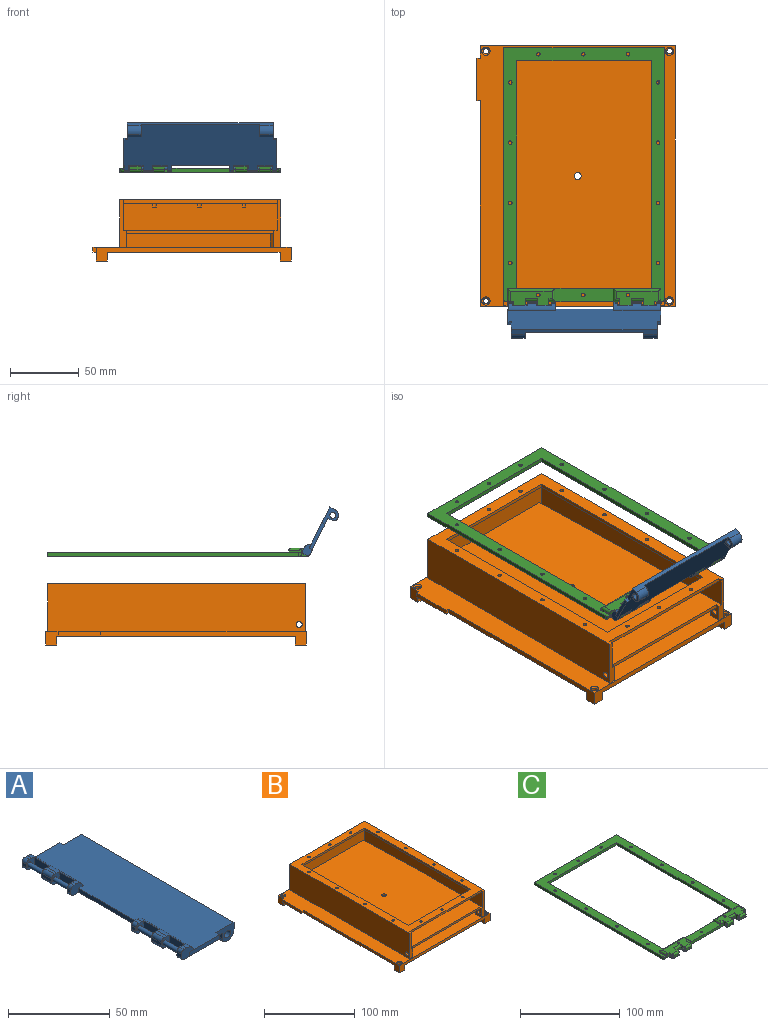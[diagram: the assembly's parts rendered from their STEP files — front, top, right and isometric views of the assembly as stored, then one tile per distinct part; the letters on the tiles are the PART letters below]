
ASSEMBLY  parts=3 mates=2
PART A: 74 faces, bbox 39.1x111x12.5 mm
  f0: plane 111x37.11mm, normal (0,0,-1), area 3582.4mm2, adj f13,f14,f15,f16,f17,f18,f19,f20
  f1: plane 3x1.73mm, normal (0,0,1), area 5.2mm2, adj f3,f17,f30,f59
  f2: plane 111x33.44mm, normal (0,0,1), area 3443.5mm2, adj f3,f13,f14,f15,f16,f32,f49,f57
  f3: cylinder r=5mm len=34mm, axis (0,1,0), area 175.9mm2, adj f1,f2,f9,f10,f13,f17,f18,f19
  f4: cylinder r=1.5mm len=3mm, axis (0,1,0), area 0.6mm2, adj f35,f56
  f5: cylinder r=1.25mm len=28.6mm, axis (0,-1,0), area 224.6mm2, adj f55,f56
  f6: cylinder r=1.5mm len=3mm, axis (0,1,0), area 0.4mm2, adj f38,f55
  f7: cylinder r=1.25mm len=28.5mm, axis (0,1,0), area 223.8mm2, adj f52,f53
  f8: cylinder r=1.5mm len=3mm, axis (0,1,0), area 4.7mm2, adj f17,f52
  f9: plane 2.5x1.73mm, normal (0,0,1), area 4.3mm2, adj f3,f13,f19,f29
  f10: plane 6.75x1.73mm, normal (0,0,1), area 11.7mm2, adj f3,f18,f21,f31
  f11: plane 3x1.9mm, normal (0,0,1), area 5.7mm2, adj f32,f35,f48,f49
  f12: plane 6.75x1.9mm, normal (0,0,1), area 12.8mm2, adj f40,f42,f46,f49
  f13: plane 8.5x6mm, normal (0,-1,0), area 37.3mm2, adj f0,f2,f3,f9,f16,f25,f26,f29
  f14: plane 8.67x6mm, normal (0,1,0), area 38.4mm2, adj f0,f2,f16,f33,f37,f44,f47,f49
  f15: plane 2.5x0.08mm, normal (-1,0,0), area 0.2mm2, adj f0,f2,f32,f62
  f16: plane 42.42x2.5mm, normal (-1,0,0), area 106mm2, adj f0,f2,f13,f14
  f17: plane 6x5.5mm, normal (0,-1,0), area 24mm2, adj f0,f1,f3,f8,f20,f24,f27,f30
  f18: plane 6x5.5mm, normal (0,1,0), area 24mm2, adj f0,f3,f10,f20,f23,f28,f31,f51
  f19: plane 6x5.5mm, normal (0,1,0), area 24mm2, adj f0,f3,f9,f22,f25,f26,f29,f54
  f20: plane 10.88x5.68mm, normal (-1,0,0), area 61.7mm2, adj f0,f3,f17,f18
  f21: plane 6x5.5mm, normal (0,-1,0), area 24mm2, adj f0,f3,f10,f22,f23,f28,f31,f51
  f22: plane 10.88x5.68mm, normal (-1,0,0), area 61.7mm2, adj f0,f3,f19,f21
  f23: plane 6.75x2mm, normal (-1,0,0), area 13.5mm2, adj f18,f21,f28,f31
  f24: plane 3x2mm, normal (-1,0,0), area 6mm2, adj f17,f27,f30,f59
  f25: plane 2.5x2mm, normal (-1,0,0), area 5mm2, adj f13,f19,f26,f29
  f26: cylinder r=2mm len=2.5mm, axis (0,1,0), area 7.9mm2, adj f0,f13,f19,f25
  f27: cylinder r=2mm len=3mm, axis (0,1,0), area 9.4mm2, adj f0,f17,f24,f59
  f28: cylinder r=2mm len=6.75mm, axis (0,1,0), area 21.2mm2, adj f0,f18,f21,f23
  f29: cylinder r=2mm len=2.5mm, axis (0,-1,0), area 7.9mm2, adj f9,f13,f19,f25
  f30: cylinder r=2mm len=3mm, axis (0,-1,0), area 9.4mm2, adj f1,f17,f24,f59
  f31: cylinder r=2mm len=6.75mm, axis (0,-1,0), area 21.2mm2, adj f10,f18,f21,f23
  f32: plane 8.67x6mm, normal (0,-1,0), area 38.4mm2, adj f0,f2,f11,f15,f36,f45,f48,f49
  f33: plane 3x1.9mm, normal (0,0,1), area 5.7mm2, adj f14,f38,f47,f49
  f34: plane 10.88x5.74mm, normal (-1,0,0), area 62.4mm2, adj f0,f35,f42,f49
  f35: plane 6x5.5mm, normal (0,1,0), area 24.1mm2, adj f0,f4,f11,f34,f36,f45,f48,f49
  f36: plane 3x2mm, normal (-1,0,0), area 6mm2, adj f32,f35,f45,f48
  f37: plane 3x2mm, normal (-1,0,0), area 6mm2, adj f14,f38,f44,f47
  f38: plane 6x5.5mm, normal (0,-1,0), area 24.1mm2, adj f0,f6,f33,f37,f39,f44,f47,f49
  f39: plane 10.88x5.74mm, normal (-1,0,0), area 62.4mm2, adj f0,f38,f40,f49
  f40: plane 6x5.5mm, normal (0,1,0), area 24.1mm2, adj f0,f12,f39,f41,f43,f46,f49,f50
  f41: plane 6.75x2mm, normal (-1,0,0), area 13.5mm2, adj f40,f42,f43,f46
  f42: plane 6x5.5mm, normal (0,-1,0), area 24.1mm2, adj f0,f12,f34,f41,f43,f46,f49,f50
  f43: cylinder r=2mm len=6.75mm, axis (0,-1,0), area 21.2mm2, adj f0,f40,f41,f42
  f44: cylinder r=2mm len=3mm, axis (0,-1,0), area 9.4mm2, adj f0,f14,f37,f38
  f45: cylinder r=2mm len=3mm, axis (0,-1,0), area 9.4mm2, adj f0,f32,f35,f36
  f46: cylinder r=2mm len=6.75mm, axis (0,1,0), area 21.2mm2, adj f12,f40,f41,f42
  f47: cylinder r=2mm len=3mm, axis (0,1,0), area 9.4mm2, adj f14,f33,f37,f38
  f48: cylinder r=2mm len=3mm, axis (0,1,0), area 9.4mm2, adj f11,f32,f35,f36
  f49: cylinder r=5mm len=34.5mm, axis (0,1,0), area 183mm2, adj f2,f11,f12,f14,f32,f33,f34,f35
  f50: cylinder r=1.5mm len=6.75mm, axis (0,1,0), area 63.6mm2, adj f40,f42
  f51: cylinder r=1.5mm len=6.75mm, axis (0,1,0), area 63.6mm2, adj f18,f21
  f52: plane 3x3mm, normal (0,-1,0), area 2.2mm2, adj f7,f8
  f53: plane 3x3mm, normal (0,1,0), area 2.2mm2, adj f7,f54
  f54: cylinder r=1.5mm len=3mm, axis (0,-1,0), area 4.7mm2, adj f19,f53
  f55: plane 3x3mm, normal (0,-1,0), area 2.2mm2, adj f5,f6
  f56: plane 3x3mm, normal (0,1,0), area 2.2mm2, adj f4,f5
  f57: plane 12.56x9mm, normal (0,1,0), area 61.9mm2, adj f0,f2,f58,f63,f67,f68,f71,f73
  f58: plane 2.5x2.5mm, normal (1,0,0), area 6.3mm2, adj f0,f2,f57,f59
  f59: plane 26.38x6mm, normal (0,1,0), area 89.5mm2, adj f0,f1,f2,f3,f24,f27,f30,f58
  f60: plane 12.56x9mm, normal (0,-1,0), area 61.9mm2, adj f0,f2,f61,f63,f65,f69,f70,f72
  f61: plane 2.5x2.5mm, normal (1,0,0), area 6.3mm2, adj f0,f2,f60,f62
  f62: plane 20.88x2.5mm, normal (0,-1,0), area 52.2mm2, adj f0,f2,f15,f61
  f63: plane 106x4mm, normal (1,0,0), area 295mm2, adj f0,f2,f57,f60,f64,f66,f70,f71
  f64: plane 8x6.5mm, normal (0,1,0), area 30.5mm2, adj f0,f63,f65,f69,f70,f72
  f65: plane 10x3.5mm, normal (-1,0,0), area 35mm2, adj f0,f60,f64,f72
  f66: plane 8x6.5mm, normal (0,-1,0), area 30.5mm2, adj f0,f63,f67,f68,f71,f73
  f67: plane 10x3.5mm, normal (-1,0,0), area 35mm2, adj f0,f57,f66,f73
  f68: cylinder r=2.12mm len=10mm, axis (0,-1,0), area 133.5mm2, adj f57,f66
  f69: cylinder r=2.12mm len=10mm, axis (0,-1,0), area 133.5mm2, adj f60,f64
  f70: cylinder r=5mm len=10mm, axis (0,1,0), area 78.5mm2, adj f60,f63,f64,f72
  f71: cylinder r=5mm len=10mm, axis (0,1,0), area 78.5mm2, adj f57,f63,f66,f73
  f72: cylinder r=3mm len=10mm, axis (0,-1,0), area 47.1mm2, adj f60,f64,f65,f70
  f73: cylinder r=3mm len=10mm, axis (0,-1,0), area 47.1mm2, adj f57,f66,f67,f71
PART B: 99 faces, bbox 143.9x189.5x44.5 mm
  f0: plane 10x9mm, normal (-1,0,0), area 83.5mm2, adj f14,f15,f16,f34,f36,f96
  f1: plane 34.5x5mm, normal (0,-1,0), area 117.5mm2, adj f3,f9,f11,f15,f30,f95
  f2: plane 10x2.5mm, normal (0,1,0), area 25mm2, adj f12,f15,f43,f95
  f3: plane 184.5x112mm, normal (0,0,1), area 20261.5mm2, adj f1,f7,f8,f9,f13,f48,f49,f50
  f4: cylinder r=2.12mm len=5mm, axis (1,0,0), area 66.8mm2, adj f30,f95
  f5: plane 10x2.5mm, normal (0,1,0), area 25mm2, adj f12,f15,f46,f94
  f6: cylinder r=2.12mm len=5mm, axis (1,0,0), area 66.8mm2, adj f29,f94
  f7: plane 184.5x22mm, normal (1,0,0), area 3573.8mm2, adj f3,f8,f10,f11,f13,f53,f86,f87
  f8: plane 112x33mm, normal (0,-1,0), area 2193.9mm2, adj f3,f7,f9,f10,f47,f49,f80,f81
  f9: plane 184.5x35.5mm, normal (-1,0,0), area 4781.7mm2, adj f1,f3,f8,f10,f11,f47,f48,f53
  f10: plane 182.35x112.7mm, normal (0,0,-1), area 4097.5mm2, adj f7,f8,f9,f53,f54,f55,f56,f57
  f11: plane 187x117mm, normal (0,0,1), area 5305.7mm2, adj f1,f7,f9,f13,f28,f29,f30,f53
  f12: plane 182x112mm, normal (0,0,-1), area 19887mm2, adj f2,f5,f43,f44,f45,f46,f50,f52
  f13: plane 34.5x5mm, normal (0,-1,0), area 117.5mm2, adj f3,f7,f11,f15,f29,f94
  f14: plane 189.5x143.91mm, normal (0,0,-1), area 26599.2mm2, adj f0,f16,f17,f18,f22,f31,f32,f34
  f15: plane 189.5x143.91mm, normal (0,0,1), area 25037.4mm2, adj f0,f1,f2,f5,f13,f16,f17,f18
  f16: plane 141.41x10mm, normal (0,1,0), area 598.9mm2, adj f0,f14,f15,f22,f31,f33,f35,f36
  f17: plane 149.7x10mm, normal (-1,0,0), area 576mm2, adj f14,f15,f18,f40,f42,f97
  f18: plane 141.41x10mm, normal (0,-1,0), area 598.9mm2, adj f14,f15,f17,f22,f37,f39,f41,f42
  f19: cylinder r=2mm len=9mm, axis (0,0,-1), area 113.1mm2, adj f26,f42
  f20: cylinder r=2mm len=9mm, axis (0,0,-1), area 113.1mm2, adj f27,f39
  f21: cylinder r=2mm len=9mm, axis (0,0,-1), area 113.1mm2, adj f24,f33
  f22: plane 189.5x10mm, normal (1,0,0), area 767.2mm2, adj f14,f15,f16,f18,f32,f33,f38,f39
  f23: cylinder r=2mm len=9mm, axis (0,0,-1), area 113.1mm2, adj f25,f36
  f24: cone r=2mm half-angle=45deg, axis (0,0,1), area 22.2mm2, adj f15,f21
  f25: cone r=2mm half-angle=45deg, axis (0,0,1), area 22.2mm2, adj f15,f23
  f26: cone r=2mm half-angle=45deg, axis (0,0,1), area 22.2mm2, adj f15,f19
  f27: cone r=2mm half-angle=45deg, axis (0,0,1), area 22.2mm2, adj f15,f20
  f28: plane 117x34.5mm, normal (0,1,0), area 4036.5mm2, adj f11,f15,f29,f30
  f29: plane 187x34.5mm, normal (-1,0,0), area 6437.3mm2, adj f6,f11,f13,f15,f28
  f30: plane 187x34.5mm, normal (1,0,0), area 6437.3mm2, adj f1,f4,f11,f15,f28
  f31: plane 8x6.5mm, normal (-1,0,0), area 52mm2, adj f14,f16,f32,f33
  f32: plane 8x6.5mm, normal (0,-1,0), area 52mm2, adj f14,f22,f31,f33
  f33: plane 8x8mm, normal (0,0,-1), area 51.4mm2, adj f16,f21,f22,f31,f32
  f34: plane 8x6.5mm, normal (0,-1,0), area 52mm2, adj f0,f14,f35,f36
  f35: plane 8x6.5mm, normal (1,0,0), area 52mm2, adj f14,f16,f34,f36
  f36: plane 8x8mm, normal (0,0,-1), area 51.4mm2, adj f0,f16,f23,f34,f35
  f37: plane 8x6.5mm, normal (-1,0,0), area 52mm2, adj f14,f18,f38,f39
  f38: plane 8x6.5mm, normal (0,1,0), area 52mm2, adj f14,f22,f37,f39
  f39: plane 8x8mm, normal (0,0,-1), area 51.4mm2, adj f18,f20,f22,f37,f38
  f40: plane 8x6.5mm, normal (0,1,0), area 52mm2, adj f14,f17,f41,f42
  f41: plane 8x6.5mm, normal (1,0,0), area 52mm2, adj f14,f18,f40,f42
  f42: plane 8x8mm, normal (0,0,-1), area 51.4mm2, adj f17,f18,f19,f40,f41
  f43: plane 170x10mm, normal (-1,-0.03,0), area 1700.7mm2, adj f2,f12,f15,f44
  f44: plane 10x6mm, normal (-1,0,0), area 60mm2, adj f12,f15,f43,f45
  f45: plane 107.09x10mm, normal (0,-1,0), area 1070.9mm2, adj f12,f15,f44,f46
  f46: plane 176x10mm, normal (1,0,0), area 1760mm2, adj f5,f12,f15,f45
  f47: plane 89.48x2.41mm, normal (0,0,1), area 115.2mm2, adj f8,f9,f48,f49
  f48: plane 83.51x13.5mm, normal (1,0.03,0), area 1127.9mm2, adj f3,f9,f47,f49
  f49: plane 13.5x5.96mm, normal (1,0,0), area 80.5mm2, adj f3,f8,f47,f48
  f50: plane 107x2.5mm, normal (0,-1,0), area 267.5mm2, adj f3,f12,f94,f95
  f51: cylinder r=2.51mm len=5.02mm, axis (0,0,1), area 55.2mm2, adj f14,f15
  f52: cylinder r=2.51mm len=5.02mm, axis (0,0,1), area 39.4mm2, adj f3,f12
  f53: plane 112x2.5mm, normal (0,-1,0), area 280mm2, adj f7,f9,f10,f11
  f54: plane 165.5x2.5mm, normal (1,0,0), area 413.8mm2, adj f10,f11,f55,f57
  f55: plane 98x2.5mm, normal (0,1,0), area 245mm2, adj f10,f11,f54,f56
  f56: plane 165.5x2.5mm, normal (-1,0,0), area 413.8mm2, adj f10,f11,f55,f57
  f57: plane 98x2.5mm, normal (0,-1,0), area 245mm2, adj f10,f11,f54,f56
  f58: cylinder r=1.3mm len=2.6mm, axis (0,0,1), area 20.4mm2, adj f10,f11
  f59: cylinder r=1.3mm len=2.6mm, axis (0,0,1), area 20.4mm2, adj f10,f11
  f60: cylinder r=1.3mm len=2.6mm, axis (0,0,1), area 20.4mm2, adj f10,f11
  f61: cylinder r=1.3mm len=2.6mm, axis (0,0,1), area 20.4mm2, adj f10,f11
  f62: cylinder r=1.3mm len=2.6mm, axis (0,0,1), area 20.4mm2, adj f10,f11
  f63: cylinder r=1.3mm len=2.6mm, axis (0,0,1), area 20.4mm2, adj f10,f11
  f64: cylinder r=1.3mm len=2.6mm, axis (0,0,1), area 20.4mm2, adj f10,f11
  f65: cylinder r=1.3mm len=2.6mm, axis (0,0,1), area 20.4mm2, adj f10,f11
  f66: cylinder r=1.3mm len=2.6mm, axis (0,0,1), area 20.4mm2, adj f10,f11
  f67: cylinder r=1.3mm len=2.6mm, axis (0,0,1), area 20.4mm2, adj f10,f11
  f68: cylinder r=1.3mm len=2.6mm, axis (0,0,1), area 20.4mm2, adj f10,f11
  f69: cylinder r=1.3mm len=2.6mm, axis (0,0,1), area 20.4mm2, adj f10,f11
  f70: cylinder r=1.3mm len=2.6mm, axis (0,0,1), area 20.4mm2, adj f10,f11
  f71: cylinder r=1.3mm len=2.6mm, axis (0,0,1), area 20.4mm2, adj f10,f11
  f72: cylinder r=2.6mm len=2.9mm, axis (0,0,1), area 7.9mm2, adj f9,f10,f73
  f73: plane 2.61x0.35mm, normal (0,0,1), area 0.6mm2, adj f9,f72
  f74: cylinder r=2.6mm len=2.9mm, axis (0,0,1), area 7.9mm2, adj f9,f10,f75
  f75: plane 2.61x0.35mm, normal (0,0,1), area 0.6mm2, adj f9,f74
  f76: cylinder r=2.6mm len=2.9mm, axis (0,0,1), area 7.9mm2, adj f9,f10,f77
  f77: plane 2.61x0.35mm, normal (0,0,1), area 0.6mm2, adj f9,f76
  f78: cylinder r=2.6mm len=2.9mm, axis (0,0,1), area 7.9mm2, adj f9,f10,f79
  f79: plane 2.61x0.35mm, normal (0,0,1), area 0.6mm2, adj f9,f78
  f80: cylinder r=2.6mm len=2.9mm, axis (0,0,1), area 7.9mm2, adj f8,f10,f81
  f81: plane 2.61x0.35mm, normal (0,0,1), area 0.6mm2, adj f8,f80
  f82: cylinder r=2.6mm len=2.9mm, axis (0,0,1), area 7.9mm2, adj f8,f10,f83
  f83: plane 2.61x0.35mm, normal (0,0,1), area 0.6mm2, adj f8,f82
  f84: cylinder r=2.6mm len=2.9mm, axis (0,0,1), area 7.9mm2, adj f8,f10,f85
  f85: plane 2.61x0.35mm, normal (0,0,1), area 0.6mm2, adj f8,f84
  f86: cylinder r=2.6mm len=2.9mm, axis (0,0,1), area 7.9mm2, adj f7,f10,f87
  f87: plane 2.61x0.35mm, normal (0,0,1), area 0.6mm2, adj f7,f86
  f88: cylinder r=2.6mm len=2.9mm, axis (0,0,1), area 7.9mm2, adj f7,f10,f89
  f89: plane 2.61x0.35mm, normal (0,0,1), area 0.6mm2, adj f7,f88
  f90: cylinder r=2.6mm len=2.9mm, axis (0,0,1), area 7.9mm2, adj f7,f10,f91
  f91: plane 2.61x0.35mm, normal (0,0,1), area 0.6mm2, adj f7,f90
  f92: cylinder r=2.6mm len=2.9mm, axis (0,0,1), area 7.9mm2, adj f7,f10,f93
  f93: plane 2.61x0.35mm, normal (0,0,1), area 0.6mm2, adj f7,f92
  f94: plane 12.5x8.5mm, normal (1,0,0), area 77.1mm2, adj f3,f5,f6,f12,f13,f15,f50
  f95: plane 12.5x8.5mm, normal (-1,0,0), area 77.1mm2, adj f1,f2,f3,f4,f12,f15,f50
  f96: plane 3.5x2.5mm, normal (0,1,0), area 8.7mm2, adj f0,f14,f15,f98
  f97: plane 3.5x2.5mm, normal (0,-1,0), area 8.7mm2, adj f14,f15,f17,f98
  f98: plane 30.8x3.5mm, normal (-1,0,0), area 107.8mm2, adj f14,f15,f96,f97
PART C: 77 faces, bbox 117x190.5x6 mm
  f0: plane 5.13x4mm, normal (0,-1,0), area 12.3mm2, adj f5,f34,f45,f47,f48,f70
  f1: plane 8.75x2mm, normal (0,-1,0), area 17.5mm2, adj f42,f44,f49,f50
  f2: plane 8.75x2mm, normal (0,-1,0), area 17.5mm2, adj f36,f38,f56,f57
  f3: plane 5.13x4mm, normal (0,-1,0), area 12.3mm2, adj f5,f31,f35,f51,f71,f72
  f4: plane 42.5x9.5mm, normal (0,0,1), area 398.4mm2, adj f7,f12,f22,f29,f32
  f5: plane 184.5x117mm, normal (0,0,1), area 4249.8mm2, adj f0,f3,f6,f8,f9,f10,f11,f12
  f6: plane 182.5x3mm, normal (-1,0,0), area 547.5mm2, adj f5,f27,f28,f72
  f7: plane 51.25x4mm, normal (0,-1,0), area 162.5mm2, adj f4,f28,f29,f32,f39,f41,f55,f66
  f8: plane 182.5x3mm, normal (1,0,0), area 547.5mm2, adj f5,f27,f28,f47
  f9: plane 165.5x3mm, normal (1,0,0), area 496.5mm2, adj f5,f10,f12,f28
  f10: plane 98x3mm, normal (0,-1,0), area 294mm2, adj f5,f9,f11,f28
  f11: plane 165.5x3mm, normal (-1,0,0), area 496.5mm2, adj f5,f10,f12,f28
  f12: plane 111.5x4mm, normal (0,1,0), area 363mm2, adj f4,f5,f9,f11,f28,f29,f30,f32
  f13: cylinder r=1.3mm len=3mm, axis (0,0,-1), area 24.5mm2, adj f5,f28
  f14: cylinder r=1.3mm len=3mm, axis (0,0,-1), area 24.5mm2, adj f5,f28
  f15: cylinder r=1.3mm len=3mm, axis (0,0,-1), area 24.5mm2, adj f5,f28
  f16: cylinder r=1.3mm len=3mm, axis (0,0,-1), area 24.5mm2, adj f5,f28
  f17: cylinder r=1.3mm len=3mm, axis (0,0,-1), area 24.5mm2, adj f5,f28
  f18: cylinder r=1.3mm len=3mm, axis (0,0,-1), area 24.5mm2, adj f5,f28
  f19: cylinder r=1.3mm len=3mm, axis (0,0,-1), area 24.5mm2, adj f5,f28
  f20: cylinder r=1.3mm len=3mm, axis (0,0,-1), area 24.5mm2, adj f5,f28
  f21: cylinder r=1.3mm len=6mm, axis (0,0,-1), area 49mm2, adj f28,f31
  f22: cylinder r=1.3mm len=3mm, axis (0,0,-1), area 24.5mm2, adj f4,f28
  f23: cylinder r=1.3mm len=6mm, axis (0,0,-1), area 49mm2, adj f28,f34
  f24: cylinder r=1.3mm len=3mm, axis (0,0,-1), area 24.5mm2, adj f5,f28
  f25: cylinder r=1.3mm len=3mm, axis (0,0,-1), area 24.5mm2, adj f5,f28
  f26: cylinder r=1.3mm len=3mm, axis (0,0,-1), area 24.5mm2, adj f5,f28
  f27: plane 117x3mm, normal (0,1,0), area 351mm2, adj f5,f6,f8,f28
  f28: plane 188.5x117mm, normal (0,0,-1), area 5365.7mm2, adj f6,f7,f8,f9,f10,f11,f12,f13
  f29: plane 9.5x1mm, normal (1,0,0), area 9.5mm2, adj f4,f7,f12,f54
  f30: plane 7.5x1mm, normal (-1,0,0), area 7.5mm2, adj f5,f12,f51,f52
  f31: plane 30.5x11.5mm, normal (0,0,1), area 269.2mm2, adj f3,f21,f35,f36,f38,f39,f52,f53
  f32: plane 9.5x1mm, normal (-1,0,0), area 9.5mm2, adj f4,f7,f12,f67
  f33: plane 7.5x1mm, normal (1,0,0), area 7.5mm2, adj f5,f12,f69,f70
  f34: plane 30.5x11.5mm, normal (0,0,1), area 269.2mm2, adj f0,f23,f41,f42,f44,f45,f49,f59
  f35: plane 8x6mm, normal (-1,0,0), area 28.1mm2, adj f3,f28,f31,f37,f64,f65,f71,f76
  f36: plane 8x6mm, normal (1,0,0), area 28.9mm2, adj f2,f28,f31,f37,f56,f57,f64,f65
  f37: plane 8.5x2mm, normal (0,-1,0), area 17mm2, adj f35,f36,f64,f65
  f38: plane 8x6mm, normal (-1,0,0), area 28.9mm2, adj f2,f28,f31,f40,f56,f57,f62,f63
  f39: plane 8x6mm, normal (1,0,0), area 28.1mm2, adj f7,f28,f31,f40,f55,f62,f63,f75
  f40: plane 8.5x2mm, normal (0,-1,0), area 17mm2, adj f38,f39,f62,f63
  f41: plane 8x6mm, normal (-1,0,0), area 28.1mm2, adj f7,f28,f34,f43,f60,f61,f66,f74
  f42: plane 8x6mm, normal (1,0,0), area 28.9mm2, adj f1,f28,f34,f43,f49,f50,f60,f61
  f43: plane 8.5x2mm, normal (0,-1,0), area 17mm2, adj f41,f42,f60,f61
  f44: plane 8x6mm, normal (-1,0,0), area 28.9mm2, adj f1,f28,f34,f46,f49,f50,f58,f59
  f45: plane 8x6mm, normal (1,0,0), area 28.1mm2, adj f0,f28,f34,f46,f48,f58,f59,f73
  f46: plane 8.5x2mm, normal (0,-1,0), area 17mm2, adj f44,f45,f58,f59
  f47: cylinder r=2mm len=3mm, axis (0,0,1), area 7.1mm2, adj f0,f5,f8,f48
  f48: cylinder r=2mm len=7.13mm, axis (1,0,0), area 20.1mm2, adj f0,f28,f45,f47
  f49: cylinder r=2mm len=8.75mm, axis (-1,0,0), area 27.5mm2, adj f1,f34,f42,f44
  f50: cylinder r=2mm len=8.75mm, axis (1,0,0), area 27.5mm2, adj f1,f28,f42,f44
  f51: cylinder r=2mm len=3mm, axis (0,0,-1), area 7.1mm2, adj f3,f5,f30,f52
  f52: cylinder r=2mm len=9.5mm, axis (0,1,0), area 25.3mm2, adj f30,f31,f51,f53
  f53: cylinder r=2mm len=34.5mm, axis (1,0,0), area 103.8mm2, adj f12,f31,f52,f54
  f54: cylinder r=2mm len=9.5mm, axis (0,-1,0), area 25.3mm2, adj f29,f31,f53,f55
  f55: cylinder r=2mm len=4.38mm, axis (-1,0,0), area 11.5mm2, adj f7,f31,f39,f54
  f56: cylinder r=2mm len=8.75mm, axis (-1,0,0), area 27.5mm2, adj f2,f31,f36,f38
  f57: cylinder r=2mm len=8.75mm, axis (1,0,0), area 27.5mm2, adj f2,f28,f36,f38
  f58: cylinder r=2mm len=8.5mm, axis (-1,0,0), area 26.7mm2, adj f28,f44,f45,f46
  f59: cylinder r=2mm len=8.5mm, axis (1,0,0), area 26.7mm2, adj f34,f44,f45,f46
  f60: cylinder r=2mm len=8.5mm, axis (-1,0,0), area 26.7mm2, adj f28,f41,f42,f43
  f61: cylinder r=2mm len=8.5mm, axis (1,0,0), area 26.7mm2, adj f34,f41,f42,f43
  f62: cylinder r=2mm len=8.5mm, axis (-1,0,0), area 26.7mm2, adj f28,f38,f39,f40
  f63: cylinder r=2mm len=8.5mm, axis (1,0,0), area 26.7mm2, adj f31,f38,f39,f40
  f64: cylinder r=2mm len=8.5mm, axis (-1,0,0), area 26.7mm2, adj f28,f35,f36,f37
  f65: cylinder r=2mm len=8.5mm, axis (1,0,0), area 26.7mm2, adj f31,f35,f36,f37
  f66: cylinder r=2mm len=4.38mm, axis (-1,0,0), area 11.5mm2, adj f7,f34,f41,f67
  f67: cylinder r=2mm len=9.5mm, axis (0,1,0), area 25.3mm2, adj f32,f34,f66,f68
  f68: cylinder r=2mm len=34.5mm, axis (1,0,0), area 103.8mm2, adj f12,f34,f67,f69
  f69: cylinder r=2mm len=9.5mm, axis (0,-1,0), area 25.3mm2, adj f33,f34,f68,f70
  f70: cylinder r=2mm len=3mm, axis (0,0,1), area 7.1mm2, adj f0,f5,f33,f69
  f71: cylinder r=2mm len=7.13mm, axis (1,0,0), area 20.1mm2, adj f3,f28,f35,f72
  f72: cylinder r=2mm len=3mm, axis (0,0,-1), area 7.1mm2, adj f3,f5,f6,f71
  f73: cylinder r=1.5mm len=8.5mm, axis (-1,0,0), area 80.1mm2, adj f44,f45
  f74: cylinder r=1.5mm len=8.5mm, axis (-1,0,0), area 80.1mm2, adj f41,f42
  f75: cylinder r=1.5mm len=8.5mm, axis (-1,0,0), area 80.1mm2, adj f38,f39
  f76: cylinder r=1.5mm len=8.5mm, axis (-1,0,0), area 80.1mm2, adj f35,f36
PLACE A rot(axis=(-0.47,-0.47,-0.75),106.1deg) t=(16.03,-105.59,74.67)mm
PLACE B t=(-27.48,-5.24,9.18)mm fixed
PLACE C t=(-13.55,-33.44,67.18)mm
MATE cylindrical A.f5 <-> C.f73  axis (-1,0,0) through (-60.9,-100.02,70.18)mm
MATE slider C.f20 <-> B.f69  axis (0,0,-1) through (-76.52,-68.52,67.18)mm
